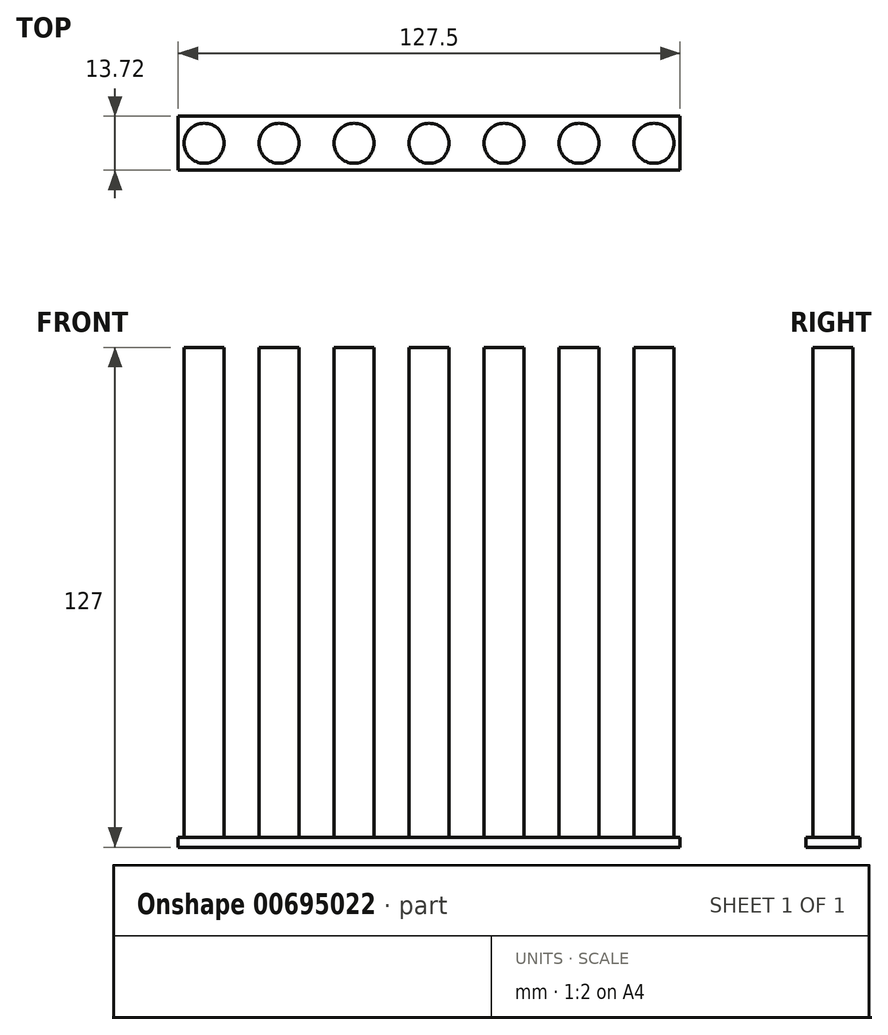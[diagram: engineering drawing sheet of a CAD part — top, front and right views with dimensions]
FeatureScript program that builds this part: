
annotation { "Feature Type Name" : "Feature", "Feature Type Description" : "" }
export const myFeature = defineFeature(function(context is Context, id is Id, definition is map)
    precondition{}
    {
        {
            var Q0;
            Q0=qCreatedBy(makeId("Top.planeOp"),FACE);
            var sketch = newSketch(context, id + "F0", { "sketchPlane" : qUnion([Q0])});
            skLineSegment(sketch, "E0.bottom", {"start": v(63.75, 6.86) * mm, "end": v(-63.75, 6.86) * mm});
            skLineSegment(sketch, "E0.top", {"start": v(63.75, -6.86) * mm, "end": v(-63.75, -6.86) * mm});
            skLineSegment(sketch, "E0.left", {"start": v(63.75, 6.86) * mm, "end": v(63.75, -6.86) * mm});
            skLineSegment(sketch, "E0.right", {"start": v(-63.75, 6.86) * mm, "end": v(-63.75, -6.86) * mm});
            skPoint(sketch, "E0.middle", {"position": v(0, 0) * mm});
            skSolve(sketch);
        }
        {
            var Q0;
            Q0 = qSketchRegion(id + "F0", true);
            extrude(context, id + "F1", {"entities" : qUnion([Q0]), "depth" : 2.54 * mm, "offsetDistance" : 25.4 * mm});
        }
        {
            var Q0;
            Q0=qCreatedBy(makeId("Top.planeOp"),FACE);
            var sketch = newSketch(context, id + "F2", { "sketchPlane" : qUnion([Q0])});
            skCircle(sketch, "E1", {"center": v(0, 0) * mm, "radius": 5.08 * mm});
            skLineSegment(sketch, "E2", {"start": v(9.53, 5.28) * mm, "end": v(9.53, -6.2) * mm, "construction": true});
            skCircle(sketch, "E3.MirrorC", {"center": v(19.05, 0) * mm, "radius": 5.08 * mm});
            skLineSegment(sketch, "E4", {"start": v(19.05, 8.72) * mm, "end": v(19.05, -10.56) * mm, "construction": true});
            skLineSegment(sketch, "E5.MirrorCS", {"start": v(28.58, 5.28) * mm, "end": v(28.58, -6.2) * mm, "construction": true});
            skCircle(sketch, "E6.MirrorC", {"center": v(38.1, 0) * mm, "radius": 5.08 * mm});
            skLineSegment(sketch, "E7.MirrorCS", {"start": v(38.1, 8.72) * mm, "end": v(38.1, -10.56) * mm, "construction": true});
            skLineSegment(sketch, "E8.MirrorCS", {"start": v(47.63, 5.28) * mm, "end": v(47.63, -6.2) * mm, "construction": true});
            skCircle(sketch, "E9.MirrorC", {"center": v(57.15, 0) * mm, "radius": 5.08 * mm});
            skCircle(sketch, "E10.MirrorC", {"center": v(-19.05, 0) * mm, "radius": 5.08 * mm});
            skCircle(sketch, "E11.MirrorC", {"center": v(-38.1, 0) * mm, "radius": 5.08 * mm});
            skCircle(sketch, "E12.MirrorC", {"center": v(-57.15, 0) * mm, "radius": 5.08 * mm});
            skSolve(sketch);
        }
        {
            var Q0;
            Q0 = qSketchRegion(id + "F2", true);
            extrude(context, id + "F3", {"entities" : qUnion([Q0]), "operationType" : NewBodyOperationType.ADD, "depth" : 127 * mm, "offsetDistance" : 25.4 * mm});
        }
    });
